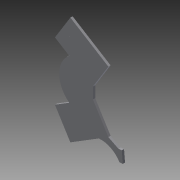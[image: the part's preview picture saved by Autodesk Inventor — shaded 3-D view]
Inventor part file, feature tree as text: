
AUTODESK INVENTOR PART (.ipt)
format: ipt  version: 2015 (Build 190159000, 159)  size: 113,664 bytes
history: native  units: mm
features: extrude x4, sketch x1
ambient origin geometry x8: Origin, YZ Plane, XZ Plane, XY Plane, X Axis, Y Axis, Z Axis, Center Point
bodies: Solid1 (feature_tree)
feature tree (5):
  sketch  "Sketch1"  dims[d5=10.0mm d6=26.0mm d7=26.0mm d8=26.0mm d9=26.0mm d10=36.0mm d12=0.2mm d13=15.0mm d14=15.0mm d15=2.0mm d16=0.0mm d20=2.0mm d21=0.0mm d22=3.0mm d23=2.0mm d24=0.0mm d25=0.2mm d26=0.2mm d27=2.0mm d28=0.0mm]
  extrude  "Extrusion1"  Depth=26.0mm
  extrude  "Extrusion2"  Depth=26.0mm
  extrude  "Extrusion3"  Depth=26.0mm
  extrude  "Extrusion4"  Depth=26.0mm
